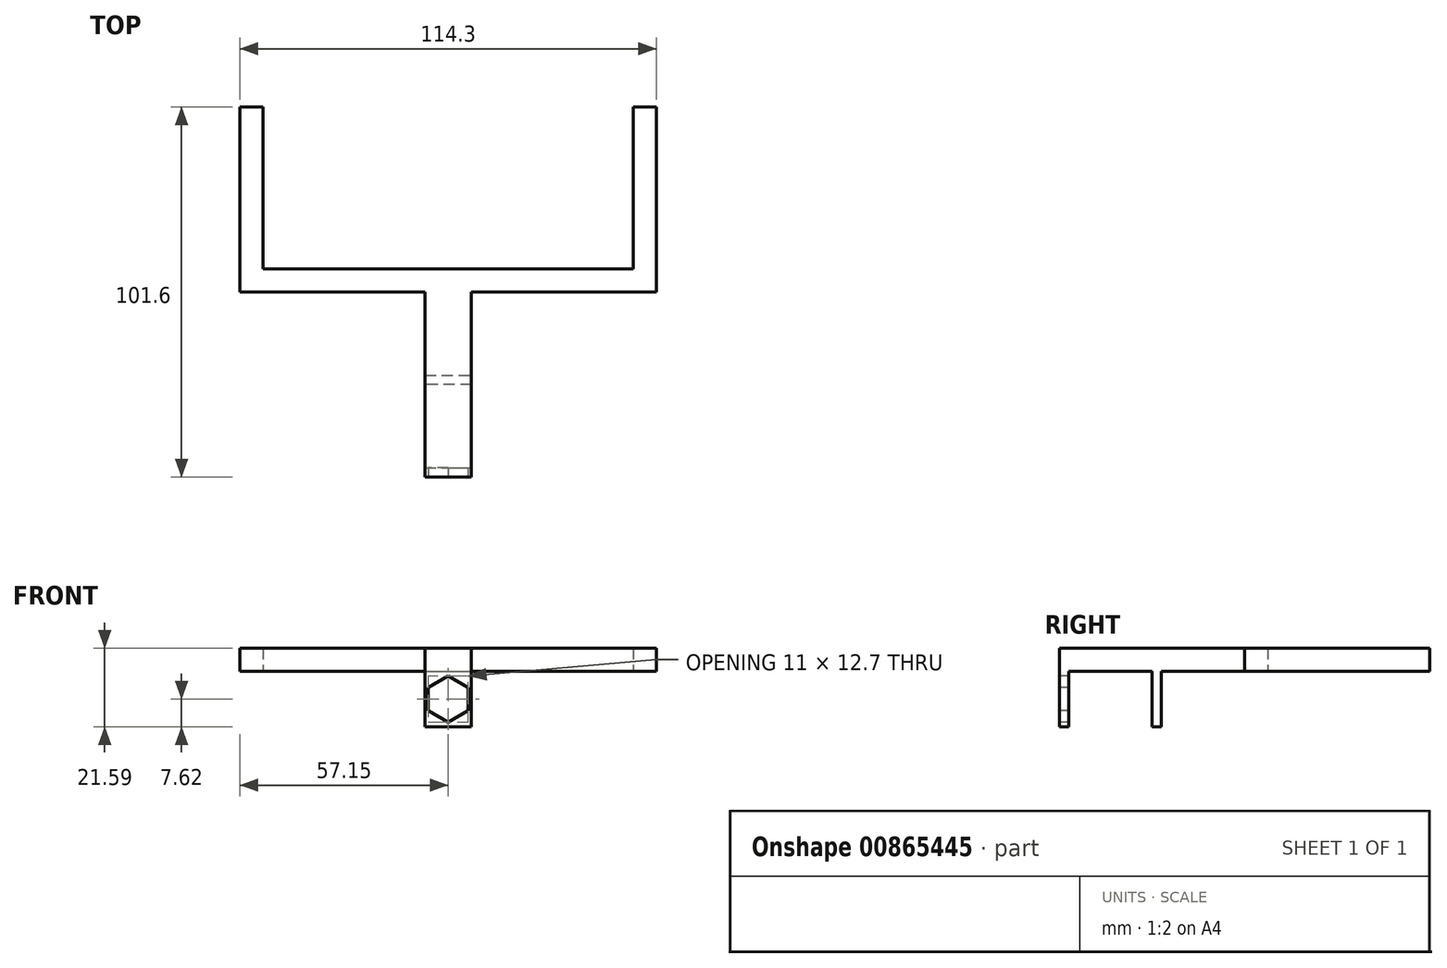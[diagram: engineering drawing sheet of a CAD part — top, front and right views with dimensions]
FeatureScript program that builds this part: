
annotation { "Feature Type Name" : "Feature", "Feature Type Description" : "" }
export const myFeature = defineFeature(function(context is Context, id is Id, definition is map)
    precondition{}
    {
        {
            var Q0;
            Q0=qCreatedBy(makeId("Top.planeOp"),FACE);
            var sketch = newSketch(context, id + "F0", { "sketchPlane" : qUnion([Q0])});
            skLineSegment(sketch, "E0", {"start": v(-6.35, -50.8) * mm, "end": v(-12.7, -50.8) * mm});
            skLineSegment(sketch, "E1", {"start": v(-6.35, -30.86) * mm, "end": v(-6.35, 80.53) * mm, "construction": true});
            skLineSegment(sketch, "E2", {"start": v(-12.7, -50.8) * mm, "end": v(-12.7, 0) * mm});
            skLineSegment(sketch, "E3", {"start": v(-12.7, 0) * mm, "end": v(-63.5, 0) * mm});
            skLineSegment(sketch, "E4", {"start": v(0, 0) * mm, "end": v(50.8, 0) * mm});
            skLineSegment(sketch, "E5", {"start": v(-63.5, 0) * mm, "end": v(-63.5, 50.8) * mm});
            skLineSegment(sketch, "E6", {"start": v(50.8, 0) * mm, "end": v(50.8, 50.8) * mm});
            skLineSegment(sketch, "E7", {"start": v(-6.35, -50.8) * mm, "end": v(0, -50.8) * mm});
            skLineSegment(sketch, "E8", {"start": v(0, -50.8) * mm, "end": v(0, 0) * mm});
            skLineSegment(sketch, "E9", {"start": v(50.8, 50.8) * mm, "end": v(44.45, 50.8) * mm});
            skLineSegment(sketch, "E10", {"start": v(-63.5, 50.8) * mm, "end": v(-57.15, 50.8) * mm});
            skLineSegment(sketch, "E11", {"start": v(-57.15, 50.8) * mm, "end": v(-57.15, 6.35) * mm});
            skLineSegment(sketch, "E12", {"start": v(-57.15, 6.35) * mm, "end": v(44.45, 6.35) * mm});
            skLineSegment(sketch, "E13", {"start": v(44.45, 50.8) * mm, "end": v(44.45, 6.35) * mm});
            skSolve(sketch);
        }
        {
            var Q0;
            Q0=makeQuery(id+"F0.imprint","IMPRINT",FACE,{"disambiguationData":[TD([[makeQuery(id+"F0.imprint","IMPRINT",EDGE,{"derivedFrom":sQuery(id+"F0.wireOp",EDGE,"E0")}),-1.0]])]});
            extrude(context, id + "F1", {"entities" : qUnion([Q0]), "depth" : 6.35 * mm, "offsetDistance" : 25.4 * mm});
        }
        {
            var Q0;
            Q0=makeQuery(id+"F1.opExtrude","CAP_FACE",FACE,{"disambiguationData":[OSD([sQuery(id+"F0.wireOp",EDGE,"E0"),sQuery(id+"F0.wireOp",EDGE,"E2"),sQuery(id+"F0.wireOp",EDGE,"E3"),sQuery(id+"F0.wireOp",EDGE,"E4"),sQuery(id+"F0.wireOp",EDGE,"E5"),sQuery(id+"F0.wireOp",EDGE,"E6"),sQuery(id+"F0.wireOp",EDGE,"E7"),sQuery(id+"F0.wireOp",EDGE,"E8"),sQuery(id+"F0.wireOp",EDGE,"E9"),sQuery(id+"F0.wireOp",EDGE,"E10"),sQuery(id+"F0.wireOp",EDGE,"E11"),sQuery(id+"F0.wireOp",EDGE,"E12"),sQuery(id+"F0.wireOp",EDGE,"E13")])],"isStart":true});
            var sketch = newSketch(context, id + "F2", { "sketchPlane" : qUnion([Q0])});
            skLineSegment(sketch, "E14", {"start": v(-6.35, 50.8) * mm, "end": v(-6.35, 25.4) * mm});
            skLineSegment(sketch, "E15", {"start": v(0, 25.4) * mm, "end": v(-12.7, 25.4) * mm});
            skLineSegment(sketch, "E16", {"start": v(-12.7, 25.4) * mm, "end": v(-12.7, 22.86) * mm});
            skLineSegment(sketch, "E17", {"start": v(-12.7, 22.86) * mm, "end": v(0, 22.86) * mm});
            skLineSegment(sketch, "E18", {"start": v(0, 22.86) * mm, "end": v(0, 25.4) * mm});
            skLineSegment(sketch, "E19", {"start": v(-12.7, 50.8) * mm, "end": v(-12.7, 48.26) * mm});
            skLineSegment(sketch, "E20", {"start": v(-12.7, 48.26) * mm, "end": v(0, 48.26) * mm});
            skLineSegment(sketch, "E21", {"start": v(0, 48.26) * mm, "end": v(0, 50.8) * mm});
            skSolve(sketch);
        }
        {
            var Q0;
            {var subQ0=sQuery(id+"F2.wireOp",EDGE,"E16");Q0=makeQuery(id+"F2.imprint","IMPRINT",FACE,{"disambiguationData":[TD([[makeQuery(id+"F2.imprint","IMPRINT",EDGE,{"derivedFrom":subQ0}),1.0]])]});}
            var Q1;
            {var subQ5=sQuery(id+"F2.wireOp",EDGE,"E19");Q1=makeQuery(id+"F2.imprint","IMPRINT",FACE,{"disambiguationData":[TD([[makeQuery(id+"F2.imprint","IMPRINT",EDGE,{"derivedFrom":subQ5}),1.0]])]});}
            var Q2;
            {var subQ5=sQuery(id+"F2.wireOp",EDGE,"E21");Q2=makeQuery(id+"F2.imprint","IMPRINT",FACE,{"disambiguationData":[TD([[makeQuery(id+"F2.imprint","IMPRINT",EDGE,{"derivedFrom":subQ5}),-1.0]])]});}
            extrude(context, id + "F3", {"entities" : qUnion([Q0, Q1, Q2]), "operationType" : NewBodyOperationType.ADD, "depth" : 15.24 * mm, "offsetDistance" : 25.4 * mm});
        }
        {
            var Q0;
            {var subQ0=sQuery(id+"F0.wireOp",EDGE,"E7");var subQ1=sQuery(id+"F0.wireOp",EDGE,"E0");Q0=makeQuery(id+"F3.boolean.opBoolean","MERGE",FACE,{"derivedFrom":[makeQuery(id+"F1.opExtrude","SWEPT_FACE",FACE,{"disambiguationData":[OSD([subQ1,subQ0])]}),makeQuery(id+"F3.opExtrude","SWEPT_FACE",FACE,{"disambiguationData":[OSD([subQ1,subQ0])]})]});}
            var sketch = newSketch(context, id + "F4", { "sketchPlane" : qUnion([Q0])});
            skLineSegment(sketch, "E22.0", {"start": v(-12.7, 0) * mm, "end": v(0, 0) * mm});
            skLineSegment(sketch, "E23", {"start": v(0, 0) * mm, "end": v(0, -15.24) * mm});
            skLineSegment(sketch, "E24", {"start": v(0, -7.62) * mm, "end": v(-6.35, -7.62) * mm, "construction": true});
            skPoint(sketch, "E24.endSnap0", {"position": v(-6.35, 0) * mm});
            skCircle(sketch, "E25.cCircle", {"center": v(-6.35, -7.62) * mm, "radius": 5.5 * mm, "construction": true});
            skLineSegment(sketch, "E25.0", {"start": v(-6.35, -13.97) * mm, "end": v(-11.85, -10.8) * mm});
            skLineSegment(sketch, "E25.1", {"start": v(-11.85, -10.8) * mm, "end": v(-11.85, -4.45) * mm});
            skLineSegment(sketch, "E25.2", {"start": v(-11.85, -4.45) * mm, "end": v(-6.35, -1.27) * mm});
            skLineSegment(sketch, "E25.3", {"start": v(-6.35, -1.27) * mm, "end": v(-0.85, -4.45) * mm});
            skLineSegment(sketch, "E25.4", {"start": v(-0.85, -4.45) * mm, "end": v(-0.85, -10.8) * mm});
            skLineSegment(sketch, "E25.5", {"start": v(-0.85, -10.8) * mm, "end": v(-6.35, -13.97) * mm});
            skPoint(sketch, "E25.0.midPoint", {"position": v(-9.1, -12.38) * mm});
            skLineSegment(sketch, "E26", {"start": v(-6.35, 0) * mm, "end": v(-6.35, -1.27) * mm, "construction": true});
            skSolve(sketch);
        }
        {
            var Q0;
            Q0=makeQuery(id+"F4.imprint","IMPRINT",FACE,{"disambiguationData":[TD([[makeQuery(id+"F4.imprint","IMPRINT",EDGE,{"derivedFrom":sQuery(id+"F4.wireOp",EDGE,"E25.0")}),-1.0]])]});
            var Q1;
            Q1=makeQuery(id+"F3.opExtrude","SWEPT_FACE",FACE,{"disambiguationData":[OSD([sQuery(id+"F2.wireOp",EDGE,"E20")])]});
            extrude(context, id + "F5", {"entities" : qUnion([Q0]), "operationType" : NewBodyOperationType.REMOVE, "endBound" : BoundingType.UP_TO_SURFACE, "oppositeDirection" : true, "depth" : 25.4 * mm, "endBoundEntityFace" : qUnion([Q1]), "offsetDistance" : 25.4 * mm});
        }
    });
